# Revit family: TSM Betonschraube Linsenkopf VZ 30 TSM-L 6
name_source: partatom
category: HLS-Bauteile
revit_build: Autodesk Revit 2017 (Build: 20190507_1515(x64)
units: mm (PartAtom-declared; Revit-internal decimal feet)

## family parameters
Arbeitsebenenbasiert = Ja
Beim Laden mit Abzugskörper schneiden = Nein
Bemaßung runder Anschluss = Durchmesser verwenden
Gemeinsam genutzt = Ja
Immer vertikal = Nein
Raumberechnungspunkt = Nein
Teiletyp = Normal

## types (1)
- TSM Betonschraube Linsenkopf VZ 30 TSM-L 6
    Artikelnummer = 2230628
    Bohrerdurchmesser = 6 mm
    Durchmesser Kopf = 15 mm
    EAN = 4250928449221
    Fabrikat = Toge
    Firma = MEFA Befestigungs- und Montagesysteme GmbH
    Form Kopf = Linsenkopf
    Gewicht = 0.01 kg
    Gewicht pro Bauteil = 0.01 kg
    Kurztext1 = Betonschraube TSM-L 6 VZ 30
    Kurztext2 = L= 28 mm Linsenkopf 15 mm
    Länge = 28 mm  [stored 0.0918635 ft]
    Material = Stahl
    Mengeneinheit = St
    Oberflaeche = Zinklamellenbeschichtet
    Vorgabe-Ansicht = 1219 mm
    max. Klemmstärke = 3 mm  [stored 0.00984252 ft]
    min. Bohrlochtiefe = 28 mm
    min. Verankerungstiefe = 25 mm
    vpe = 100 St

note: [stored X ft] marks values corroborated as IEEE doubles in the binary element streams (Revit-internal decimal feet)
